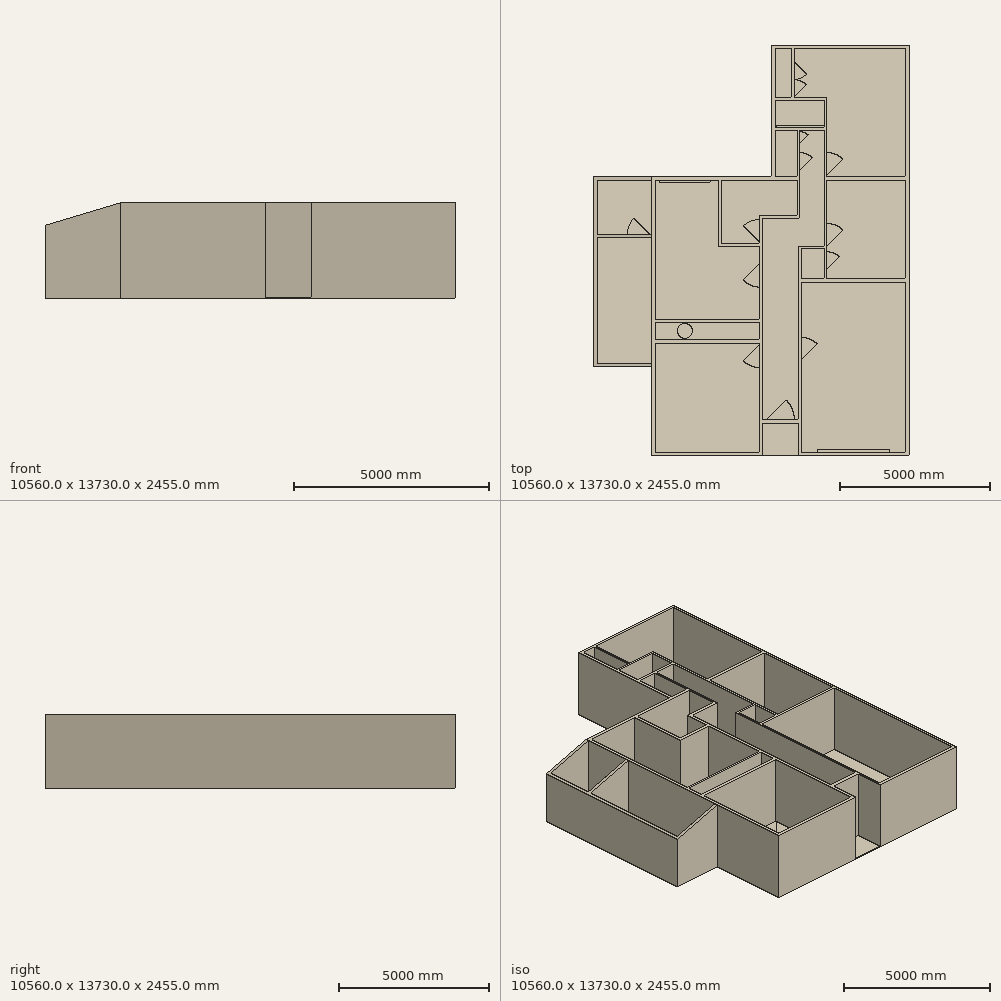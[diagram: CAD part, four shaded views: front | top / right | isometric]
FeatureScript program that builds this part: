
annotation { "Feature Type Name" : "Feature", "Feature Type Description" : "" }
export const myFeature = defineFeature(function(context is Context, id is Id, definition is map)
    precondition{}
    {
        {
            var Q0;
            Q0=qCreatedBy(makeId("Top.planeOp"),FACE);
            var sketch = newSketch(context, id + "F0", { "sketchPlane" : qUnion([Q0])});
            skLineSegment(sketch, "E0.bottom", {"start": v(0, 0) * mm, "end": v(3730, 0) * mm});
            skLineSegment(sketch, "E0.top", {"start": v(115, 3870) * mm, "end": v(3615, 3870) * mm});
            skLineSegment(sketch, "E0.left", {"start": v(0, 0) * mm, "end": v(0, 2970) * mm});
            skLineSegment(sketch, "E0.right", {"start": v(3730, 0) * mm, "end": v(3730, 1060) * mm});
            skLineSegment(sketch, "E1.bottom", {"start": v(115, 115) * mm, "end": v(3615, 115) * mm});
            skLineSegment(sketch, "E1.top", {"start": v(115, 3755) * mm, "end": v(3615, 3755) * mm});
            skLineSegment(sketch, "E1.left", {"start": v(115, 115) * mm, "end": v(115, 3755) * mm});
            skLineSegment(sketch, "E1.right", {"start": v(3615, 115) * mm, "end": v(3615, 3755) * mm});
            skLineSegment(sketch, "E2.bottom", {"start": v(3730, 1060) * mm, "end": v(4920, 1060) * mm});
            skLineSegment(sketch, "E2.left", {"start": v(3730, 1210) * mm, "end": v(3730, 7925) * mm});
            skLineSegment(sketch, "E2.right", {"start": v(4920, 1210) * mm, "end": v(4920, 7010) * mm});
            skLineSegment(sketch, "E3", {"start": v(3730, 1210) * mm, "end": v(4920, 1210) * mm});
            skLineSegment(sketch, "E4.bottom", {"start": v(5010, 5920) * mm, "end": v(5780, 5920) * mm});
            skLineSegment(sketch, "E4.top", {"start": v(4920, 0) * mm, "end": v(8625, 0) * mm});
            skLineSegment(sketch, "E4.left", {"start": v(4920, 5920) * mm, "end": v(4920, 1210) * mm});
            skLineSegment(sketch, "E4.right", {"start": v(8625, 5920) * mm, "end": v(8625, 0) * mm});
            skLineSegment(sketch, "E5.bottom", {"start": v(8510, 115) * mm, "end": v(5010, 115) * mm});
            skLineSegment(sketch, "E5.top", {"start": v(8510, 5805) * mm, "end": v(5010, 5805) * mm});
            skLineSegment(sketch, "E5.left", {"start": v(8510, 115) * mm, "end": v(8510, 5805) * mm});
            skLineSegment(sketch, "E5.right", {"start": v(5010, 115) * mm, "end": v(5010, 5805) * mm});
            skLineSegment(sketch, "E6", {"start": v(5780, 5920) * mm, "end": v(5780, 6920) * mm});
            skLineSegment(sketch, "E7", {"start": v(8625, 5920) * mm, "end": v(8625, 9335) * mm});
            skLineSegment(sketch, "E8", {"start": v(8510, 9335) * mm, "end": v(5870, 9335) * mm});
            skLineSegment(sketch, "E9.top", {"start": v(5870, 9220) * mm, "end": v(8510, 9220) * mm});
            skLineSegment(sketch, "E9.left", {"start": v(5870, 5920) * mm, "end": v(5870, 9220) * mm});
            skLineSegment(sketch, "E9.right", {"start": v(8510, 5920) * mm, "end": v(8510, 9220) * mm});
            skLineSegment(sketch, "E10.trimOffspring", {"start": v(5870, 5920) * mm, "end": v(8510, 5920) * mm});
            skLineSegment(sketch, "E11", {"start": v(5780, 7010) * mm, "end": v(4920, 7010) * mm});
            skLineSegment(sketch, "E12", {"start": v(5010, 5920) * mm, "end": v(5010, 6920) * mm});
            skLineSegment(sketch, "E13", {"start": v(5010, 6920) * mm, "end": v(5780, 6920) * mm});
            skLineSegment(sketch, "E14", {"start": v(3615, 7000) * mm, "end": v(2235, 7000) * mm});
            skLineSegment(sketch, "E15", {"start": v(2235, 7000) * mm, "end": v(2235, 9220) * mm});
            skLineSegment(sketch, "E16", {"start": v(2235, 9335) * mm, "end": v(4025, 9335) * mm});
            skLineSegment(sketch, "E17", {"start": v(4025, 9335) * mm, "end": v(4025, 13730) * mm});
            skLineSegment(sketch, "E18", {"start": v(4025, 13730) * mm, "end": v(8625, 13730) * mm});
            skLineSegment(sketch, "E19", {"start": v(8625, 9335) * mm, "end": v(8625, 13730) * mm});
            skLineSegment(sketch, "E20", {"start": v(5780, 9335) * mm, "end": v(5780, 10895) * mm});
            skLineSegment(sketch, "E21", {"start": v(5780, 11895) * mm, "end": v(4140, 11895) * mm});
            skLineSegment(sketch, "E22", {"start": v(5870, 9335) * mm, "end": v(5870, 11985) * mm});
            skLineSegment(sketch, "E23", {"start": v(5870, 11985) * mm, "end": v(4770, 11985) * mm});
            skLineSegment(sketch, "E24", {"start": v(4140, 11985) * mm, "end": v(4140, 13615) * mm});
            skLineSegment(sketch, "E25", {"start": v(4140, 13615) * mm, "end": v(4680, 13615) * mm});
            skLineSegment(sketch, "E26", {"start": v(8510, 13615) * mm, "end": v(8510, 9335) * mm});
            skLineSegment(sketch, "E27", {"start": v(4140, 9335) * mm, "end": v(4870, 9335) * mm});
            skLineSegment(sketch, "E28", {"start": v(3615, 7115) * mm, "end": v(2350, 7115) * mm});
            skLineSegment(sketch, "E29", {"start": v(2350, 7115) * mm, "end": v(2350, 9220) * mm});
            skLineSegment(sketch, "E30", {"start": v(2350, 9220) * mm, "end": v(4870, 9220) * mm});
            skLineSegment(sketch, "E31", {"start": v(4870, 9220) * mm, "end": v(4870, 8040) * mm});
            skLineSegment(sketch, "E32", {"start": v(4870, 8040) * mm, "end": v(3615, 8040) * mm});
            skLineSegment(sketch, "E33", {"start": v(4960, 7925) * mm, "end": v(4960, 9335) * mm});
            skLineSegment(sketch, "E34", {"start": v(4140, 11895) * mm, "end": v(4140, 10985) * mm});
            skLineSegment(sketch, "E35", {"start": v(4140, 10895) * mm, "end": v(5780, 10895) * mm});
            skLineSegment(sketch, "E36.trimOffspring", {"start": v(4140, 10895) * mm, "end": v(4140, 9335) * mm});
            skLineSegment(sketch, "E37.trimOffspring", {"start": v(5780, 10985) * mm, "end": v(5780, 11895) * mm});
            skLineSegment(sketch, "E38", {"start": v(4770, 13615) * mm, "end": v(4770, 11985) * mm});
            skLineSegment(sketch, "E39", {"start": v(4680, 13615) * mm, "end": v(4680, 11985) * mm});
            skLineSegment(sketch, "E40.trimOffspring", {"start": v(4770, 13615) * mm, "end": v(8510, 13615) * mm});
            skLineSegment(sketch, "E41.trimOffspring", {"start": v(4680, 11985) * mm, "end": v(4140, 11985) * mm});
            skLineSegment(sketch, "E42", {"start": v(2235, 9335) * mm, "end": v(-1935, 9335) * mm});
            skLineSegment(sketch, "E43", {"start": v(-1935, 9335) * mm, "end": v(-1935, 7285) * mm});
            skLineSegment(sketch, "E44", {"start": v(-1820, 7285) * mm, "end": v(0, 7285) * mm});
            skLineSegment(sketch, "E45", {"start": v(0, 9220) * mm, "end": v(-1820, 9220) * mm});
            skLineSegment(sketch, "E46", {"start": v(-1820, 9220) * mm, "end": v(-1820, 7400) * mm});
            skLineSegment(sketch, "E47", {"start": v(-1820, 7400) * mm, "end": v(0, 7400) * mm});
            skLineSegment(sketch, "E48", {"start": v(0, 9220) * mm, "end": v(0, 7400) * mm});
            skLineSegment(sketch, "E49", {"start": v(115, 9220) * mm, "end": v(2235, 9220) * mm});
            skLineSegment(sketch, "E50", {"start": v(4960, 9335) * mm, "end": v(4960, 10895) * mm});
            skLineSegment(sketch, "E51", {"start": v(4870, 10895) * mm, "end": v(4870, 9335) * mm});
            skLineSegment(sketch, "E52", {"start": v(115, 9220) * mm, "end": v(115, 4560) * mm});
            skLineSegment(sketch, "E53", {"start": v(3615, 3870) * mm, "end": v(3615, 4470) * mm});
            skLineSegment(sketch, "E54", {"start": v(-1935, 7285) * mm, "end": v(-1935, 2970) * mm});
            skLineSegment(sketch, "E55", {"start": v(-1935, 2970) * mm, "end": v(0, 2970) * mm});
            skLineSegment(sketch, "E56", {"start": v(-1820, 7285) * mm, "end": v(-1820, 3085) * mm});
            skLineSegment(sketch, "E57", {"start": v(-1820, 3085) * mm, "end": v(0, 3085) * mm});
            skPoint(sketch, "E58", {"position": v(4960, 10895) * mm});
            skLineSegment(sketch, "E59", {"start": v(4140, 10985) * mm, "end": v(5780, 10985) * mm});
            skLineSegment(sketch, "E60", {"start": v(3615, 7115) * mm, "end": v(3615, 8040) * mm});
            skLineSegment(sketch, "E61.trimOffspring", {"start": v(0, 7285) * mm, "end": v(0, 3870) * mm});
            skLineSegment(sketch, "E62.trimOffspring", {"start": v(3730, 7925) * mm, "end": v(4960, 7925) * mm});
            skLineSegment(sketch, "E63.trimOffspring", {"start": v(4920, 1060) * mm, "end": v(4920, 0) * mm});
            skLineSegment(sketch, "E64.trimOffspring", {"start": v(3730, 1210) * mm, "end": v(3730, 3870) * mm});
            skLineSegment(sketch, "E65.trimOffspring", {"start": v(0, 3085) * mm, "end": v(0, 3870) * mm});
            skLineSegment(sketch, "E66.trimOffspring", {"start": v(5780, 7010) * mm, "end": v(5780, 9335) * mm});
            skLineSegment(sketch, "E67", {"start": v(115, 4470) * mm, "end": v(3615, 4470) * mm});
            skLineSegment(sketch, "E68", {"start": v(115, 4560) * mm, "end": v(3615, 4560) * mm});
            skLineSegment(sketch, "E69.trimOffspring", {"start": v(115, 4470) * mm, "end": v(115, 3870) * mm});
            skLineSegment(sketch, "E70.trimOffspring", {"start": v(3615, 4560) * mm, "end": v(3615, 7000) * mm});
            skSolve(sketch);
        }
        {
            var Q0;
            Q0=makeQuery(id+"F0.imprint","IMPRINT",FACE,{"disambiguationData":[TD([[makeQuery(id+"F0.imprint","IMPRINT",EDGE,{"derivedFrom":sQuery(id+"F0.wireOp",EDGE,"E0.bottom")}),1.0]])]});
            var Q1;
            {var subQ0=sQuery(id+"F0.wireOp",EDGE,"E2.bottom");Q1=makeQuery(id+"F0.imprint","IMPRINT",FACE,{"disambiguationData":[TD([[makeQuery(id+"F0.imprint","IMPRINT",EDGE,{"derivedFrom":subQ0}),1.0]])]});}
            var Q2;
            {var subQ3=sQuery(id+"F0.wireOp",EDGE,"E4.bottom");Q2=makeQuery(id+"F0.imprint","IMPRINT",FACE,{"disambiguationData":[TD([[makeQuery(id+"F0.imprint","IMPRINT",EDGE,{"derivedFrom":subQ3}),-1.0]])]});}
            extrude(context, id + "F1", {"entities" : qUnion([Q0, Q1, Q2]), "depth" : 2430 * mm});
        }
        {
            var Q0;
            Q0=qCreatedBy(makeId("Front.planeOp"),FACE);
            var sketch = newSketch(context, id + "F2", { "sketchPlane" : qUnion([Q0])});
            skLineSegment(sketch, "E71", {"start": v(0, 0) * mm, "end": v(0, 2430) * mm});
            skLineSegment(sketch, "E72", {"start": v(0, 2430) * mm, "end": v(-1935, 1850) * mm});
            skLineSegment(sketch, "E73", {"start": v(-1935, 1850) * mm, "end": v(-1935, 3117.7) * mm});
            skLineSegment(sketch, "E74", {"start": v(-1935, 3117.7) * mm, "end": v(0, 3117.7) * mm});
            skLineSegment(sketch, "E75", {"start": v(0, 3117.7) * mm, "end": v(0, 2430) * mm});
            skSolve(sketch);
        }
        {
            var Q0;
            Q0 = qSketchRegion(id + "F2", true);
            extrude(context, id + "F3", {"entities" : qUnion([Q0]), "operationType" : NewBodyOperationType.REMOVE, "endBound" : BoundingType.THROUGH_ALL, "oppositeDirection" : true, "depth" : 25 * mm});
        }
        {
            var Q0;
            Q0=qCreatedBy(makeId("Top.planeOp"),FACE);
            var sketch = newSketch(context, id + "F4", { "sketchPlane" : qUnion([Q0])});
            skLineSegment(sketch, "E76", {"start": v(0, 0) * mm, "end": v(8625, 0) * mm});
            skLineSegment(sketch, "E77", {"start": v(8625, 0) * mm, "end": v(8625, 13730) * mm});
            skLineSegment(sketch, "E78", {"start": v(8625, 13730) * mm, "end": v(4025, 13730) * mm});
            skLineSegment(sketch, "E79", {"start": v(4025, 13730) * mm, "end": v(4025, 9335) * mm});
            skLineSegment(sketch, "E80", {"start": v(4025, 9335) * mm, "end": v(-1935, 9335) * mm});
            skLineSegment(sketch, "E81", {"start": v(-1935, 9335) * mm, "end": v(-1935, 2970) * mm});
            skLineSegment(sketch, "E82", {"start": v(-1935, 2970) * mm, "end": v(0, 2970) * mm});
            skLineSegment(sketch, "E83", {"start": v(0, 2970) * mm, "end": v(0, 0) * mm});
            skSolve(sketch);
        }
        {
            var Q0;
            Q0 = qSketchRegion(id + "F4", true);
            extrude(context, id + "F5", {"entities" : qUnion([Q0]), "operationType" : NewBodyOperationType.ADD, "oppositeDirection" : true, "depth" : 25 * mm});
        }
        {
            var Q0;
            Q0=qCreatedBy(makeId("Top.planeOp"),FACE);
            var sketch = newSketch(context, id + "F6", { "sketchPlane" : qUnion([Q0])});
            skLineSegment(sketch, "E84", {"start": v(3615, 3705) * mm, "end": v(3077.6, 3167.6) * mm});
            skArc(sketch, "E85", {"start": v(3077.6, 3167.6) * mm, "mid": v(3324.16, 3002.85) * mm, "end": v(3615, 2945) * mm});
            skLineSegment(sketch, "E86", {"start": v(3615, 6400) * mm, "end": v(3077.6, 5862.6) * mm});
            skLineSegment(sketch, "E87", {"start": v(5870, 7010) * mm, "end": v(6407.4, 7547.4) * mm});
            skLineSegment(sketch, "E88", {"start": v(5870, 6220) * mm, "end": v(6294.26, 6644.26) * mm});
            skLineSegment(sketch, "E89", {"start": v(5870, 9385) * mm, "end": v(6407.4, 9922.4) * mm});
            skLineSegment(sketch, "E90", {"start": v(3615, 7140) * mm, "end": v(3077.6, 7677.4) * mm});
            skLineSegment(sketch, "E91", {"start": v(-50, 7400) * mm, "end": v(-587.4, 7937.4) * mm});
            skLineSegment(sketch, "E92", {"start": v(3880, 1210) * mm, "end": v(4516.4, 1846.4) * mm});
            skLineSegment(sketch, "E93", {"start": v(5010, 3195) * mm, "end": v(5547.4, 3732.4) * mm});
            skLineSegment(sketch, "E94", {"start": v(5560, 200) * mm, "end": v(7960, 200) * mm});
            skLineSegment(sketch, "E95", {"start": v(7960, 200) * mm, "end": v(7960, 0) * mm});
            skLineSegment(sketch, "E96", {"start": v(5560, 200) * mm, "end": v(5560, 0) * mm});
            skLineSegment(sketch, "E97", {"start": v(5560, 0) * mm, "end": v(7960, 0) * mm});
            skLineSegment(sketch, "E98", {"start": v(265, 9135) * mm, "end": v(1985, 9135) * mm});
            skLineSegment(sketch, "E99", {"start": v(1985, 9135) * mm, "end": v(1985, 9335) * mm});
            skLineSegment(sketch, "E100", {"start": v(1985, 9335) * mm, "end": v(265, 9335) * mm});
            skLineSegment(sketch, "E101", {"start": v(265, 9335) * mm, "end": v(265, 9135) * mm});
            skLineSegment(sketch, "E102", {"start": v(4960, 9545) * mm, "end": v(5384.26, 9969.26) * mm});
            skLineSegment(sketch, "E103", {"start": v(4960, 10445) * mm, "end": v(5242.84, 10727.84) * mm});
            skLineSegment(sketch, "E104", {"start": v(4770, 13185) * mm, "end": v(5194.26, 12760.74) * mm});
            skLineSegment(sketch, "E105", {"start": v(4770, 11985) * mm, "end": v(5194.26, 12409.26) * mm});
            skLineSegment(sketch, "E106", {"start": v(1115, 4470) * mm, "end": v(1115, 3870) * mm, "construction": true});
            skCircle(sketch, "E107", {"center": v(1115, 4170) * mm, "radius": 250 * mm});
            skArc(sketch, "E108", {"start": v(4780, 1210) * mm, "mid": v(4711.5, 1554.42) * mm, "end": v(4516.4, 1846.4) * mm});
            skArc(sketch, "E109", {"start": v(5547.4, 3732.4) * mm, "mid": v(5300.84, 3897.15) * mm, "end": v(5010, 3955) * mm});
            skArc(sketch, "E110", {"start": v(6294.26, 6644.26) * mm, "mid": v(6099.61, 6774.33) * mm, "end": v(5870, 6820) * mm});
            skArc(sketch, "E111", {"start": v(6407.4, 9922.4) * mm, "mid": v(6160.84, 10087.15) * mm, "end": v(5870, 10145) * mm});
            skArc(sketch, "E112", {"start": v(3615, 7900) * mm, "mid": v(3324.16, 7842.15) * mm, "end": v(3077.6, 7677.4) * mm});
            skArc(sketch, "E113", {"start": v(3077.6, 5862.6) * mm, "mid": v(3324.16, 5697.85) * mm, "end": v(3615, 5640) * mm});
            skArc(sketch, "E114", {"start": v(-587.4, 7937.4) * mm, "mid": v(-752.15, 7690.84) * mm, "end": v(-810, 7400) * mm});
            skArc(sketch, "E115", {"start": v(5242.84, 10727.84) * mm, "mid": v(5113.07, 10814.55) * mm, "end": v(4960, 10845) * mm});
            skArc(sketch, "E116", {"start": v(5194.26, 12409.26) * mm, "mid": v(4999.61, 12539.33) * mm, "end": v(4770, 12585) * mm});
            skArc(sketch, "E117", {"start": v(4770, 12585) * mm, "mid": v(4999.61, 12630.67) * mm, "end": v(5194.26, 12760.74) * mm});
            skLineSegment(sketch, "E118", {"start": v(3880, 1210) * mm, "end": v(4780, 1210) * mm});
            skLineSegment(sketch, "E119", {"start": v(5010, 3195) * mm, "end": v(5010, 3955) * mm});
            skLineSegment(sketch, "E120", {"start": v(3615, 3705) * mm, "end": v(3615, 2945) * mm});
            skLineSegment(sketch, "E121", {"start": v(-50, 7400) * mm, "end": v(-810, 7400) * mm});
            skLineSegment(sketch, "E122", {"start": v(5870, 6220) * mm, "end": v(5870, 6820) * mm});
            skLineSegment(sketch, "E123", {"start": v(5870, 7010) * mm, "end": v(5870, 7770) * mm});
            skArc(sketch, "E124.trimOffspring", {"start": v(6407.4, 7547.4) * mm, "mid": v(6160.84, 7712.15) * mm, "end": v(5870, 7770) * mm});
            skLineSegment(sketch, "E125", {"start": v(3615, 6400) * mm, "end": v(3615, 5640) * mm});
            skLineSegment(sketch, "E126", {"start": v(3615, 7140) * mm, "end": v(3615, 7900) * mm});
            skLineSegment(sketch, "E127", {"start": v(5870, 9385) * mm, "end": v(5870, 10145) * mm});
            skLineSegment(sketch, "E128", {"start": v(4960, 10445) * mm, "end": v(4960, 10845) * mm});
            skArc(sketch, "E129", {"start": v(5384.26, 9969.26) * mm, "mid": v(5189.61, 10099.33) * mm, "end": v(4960, 10145) * mm});
            skLineSegment(sketch, "E130", {"start": v(4960, 9545) * mm, "end": v(4960, 10145) * mm});
            skLineSegment(sketch, "E131", {"start": v(4770, 13185) * mm, "end": v(4770, 12585) * mm});
            skLineSegment(sketch, "E132", {"start": v(4770, 11985) * mm, "end": v(4770, 12585) * mm});
            skLineSegment(sketch, "E133", {"start": v(5780, 10985) * mm, "end": v(5780, 11035) * mm});
            skLineSegment(sketch, "E134", {"start": v(5780, 11035) * mm, "end": v(4180, 11035) * mm});
            skLineSegment(sketch, "E135", {"start": v(4180, 11035) * mm, "end": v(4180, 10985) * mm});
            skLineSegment(sketch, "E136", {"start": v(4180, 10985) * mm, "end": v(5780, 10985) * mm});
            skSolve(sketch);
        }
        {
            var Q0;
            Q0 = qSketchRegion(id + "F6", true);
            extrude(context, id + "F7", {"entities" : qUnion([Q0]), "operationType" : NewBodyOperationType.ADD, "depth" : 0.5 * mm});
        }
    });
